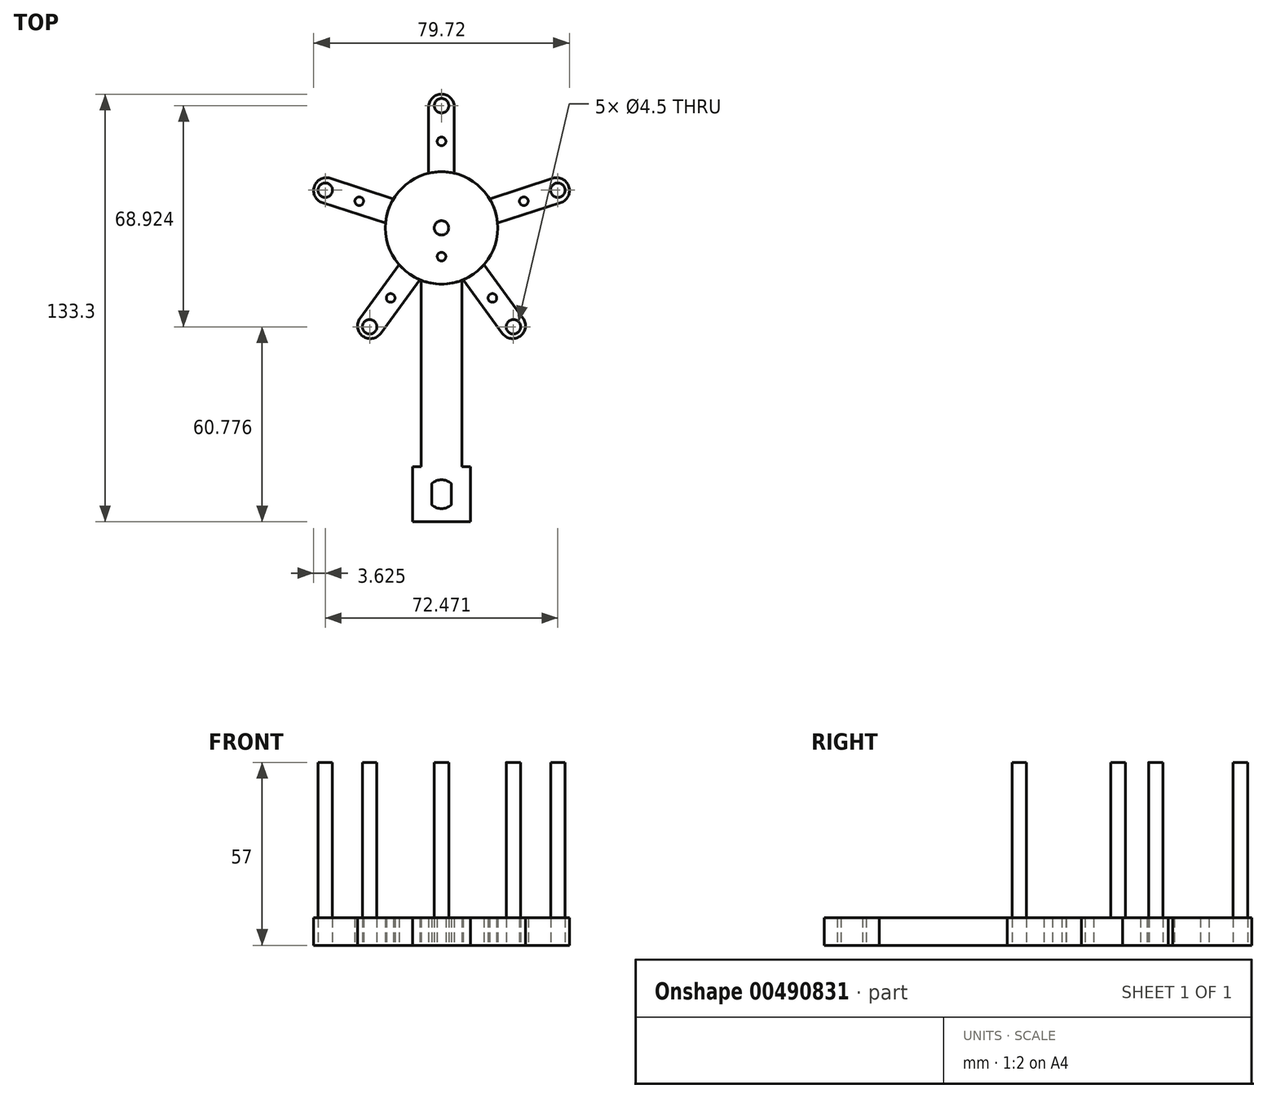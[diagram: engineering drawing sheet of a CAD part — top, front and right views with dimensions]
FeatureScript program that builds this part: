
annotation { "Feature Type Name" : "Feature", "Feature Type Description" : "" }
export const myFeature = defineFeature(function(context is Context, id is Id, definition is map)
    precondition{}
    {
        {
            var Q0;
            Q0=qCreatedBy(makeId("Top.planeOp"),FACE);
            var sketch = newSketch(context, id + "F0", { "sketchPlane" : qUnion([Q0])});
            skCircle(sketch, "E0", {"center": v(0, 0) * mm, "radius": 17.5 * mm});
            skLineSegment(sketch, "E1", {"start": v(-4, 41.7) * mm, "end": v(0, 41.7) * mm});
            skLineSegment(sketch, "E2", {"start": v(0, 41.7) * mm, "end": v(4, 41.7) * mm});
            skLineSegment(sketch, "E3", {"start": v(-6.35, -16.3) * mm, "end": v(-6.35, -74.4) * mm});
            skLineSegment(sketch, "E4", {"start": v(-6.35, -74.4) * mm, "end": v(0, -74.4) * mm});
            skLineSegment(sketch, "E5", {"start": v(0, -74.4) * mm, "end": v(6.35, -74.4) * mm});
            skLineSegment(sketch, "E6", {"start": v(6.35, -74.4) * mm, "end": v(6.35, -16.3) * mm});
            skLineSegment(sketch, "E7.bottom", {"start": v(9, -74.4) * mm, "end": v(-9, -74.4) * mm});
            skLineSegment(sketch, "E7.top", {"start": v(9, -91.6) * mm, "end": v(-9, -91.6) * mm});
            skLineSegment(sketch, "E7.left", {"start": v(9, -74.4) * mm, "end": v(9, -91.6) * mm});
            skLineSegment(sketch, "E7.right", {"start": v(-9, -74.4) * mm, "end": v(-9, -91.6) * mm});
            skPoint(sketch, "E7.middle", {"position": v(0, -83) * mm});
            skLineSegment(sketch, "E8.left", {"start": v(3, -86.35) * mm, "end": v(3, -79.65) * mm});
            skLineSegment(sketch, "E8.right", {"start": v(-3, -86.35) * mm, "end": v(-3, -79.65) * mm});
            skCircle(sketch, "E9", {"center": v(0, 38.1) * mm, "radius": 2.25 * mm});
            skLineSegment(sketch, "E10", {"start": v(4, 41.7) * mm, "end": v(4, 17.04) * mm});
            skLineSegment(sketch, "E11", {"start": v(-4, 41.7) * mm, "end": v(-4, 17.04) * mm});
            skCircle(sketch, "E12", {"center": v(-0.01, 0.01) * mm, "radius": 2.25 * mm});
            skArc(sketch, "E13", {"start": v(-3, -86.35) * mm, "mid": v(0, -87.5) * mm, "end": v(3, -86.35) * mm});
            skPoint(sketch, "E14.orphan", {"position": v(-3, -78.24) * mm});
            skPoint(sketch, "E15.orphan", {"position": v(-3, -87.33) * mm});
            skPoint(sketch, "E16.orphan", {"position": v(3, -87.76) * mm});
            skArc(sketch, "E17.trimOffspring", {"start": v(3, -79.65) * mm, "mid": v(0, -78.5) * mm, "end": v(-3, -79.65) * mm});
            skPoint(sketch, "E8.top.start.orphan", {"position": v(3, -78.67) * mm});
            skCircle(sketch, "E18", {"center": v(0, -8.94) * mm, "radius": 1.35 * mm});
            skCircle(sketch, "E19", {"center": v(0, 26.97) * mm, "radius": 1.35 * mm});
            skSolve(sketch);
        }
        {
            var Q0;
            {var subQ0=sQuery(id+"F0.wireOp",EDGE,"R38fcb1h-lACT-zBL9-eRLb-SoO7664i7xEH");Q0=makeQuery(id+"F0.imprint","IMPRINT",FACE,{"disambiguationData":[TD([[makeQuery(id+"F0.imprint","IMPRINT",EDGE,{"derivedFrom":subQ0}),-1.0]])]});}
            var Q1;
            {var subQ0=sQuery(id+"F0.wireOp",EDGE,"E0");var subQ1=makeQuery(id+"F0.imprint","INTERSECT",VERTEX,{"derivedFrom":[subQ0,sQuery(id+"F0.wireOp",EDGE,"R38fcb1h-lACT-zBL9-eRLb-SoO7664i7xEH")]});Q1=makeQuery(id+"F0.imprint","IMPRINT",FACE,{"disambiguationData":[TD([[makeQuery(id+"F0.imprint","IMPRINT",EDGE,{"disambiguationData":[TD([[subQ1,1.0]])],"derivedFrom":subQ0}),1.0]])]});}
            extrude(context, id + "F1", {"entities" : qUnion([Q0, Q1]), "depth" : 8.6 * mm});
        }
        {
            var Q0;
            {var subQ0=sQuery(id+"F0.wireOp",EDGE,"E3");Q0=makeQuery(id+"F0.imprint","IMPRINT",FACE,{"disambiguationData":[TD([[makeQuery(id+"F0.imprint","IMPRINT",EDGE,{"derivedFrom":subQ0}),1.0]])]});}
            var Q1;
            Q1=makeQuery(id+"F0.imprint","IMPRINT",FACE,{"disambiguationData":[TD([[makeQuery(id+"F0.imprint","IMPRINT",EDGE,{"derivedFrom":sQuery(id+"F0.wireOp",EDGE,"E7.top")}),-1.0]])]});
            extrude(context, id + "F2", {"entities" : qUnion([Q0, Q1]), "depth" : 8.6 * mm});
        }
        {
            var Q0;
            Q0=makeQuery(id+"F0.imprint","IMPRINT",FACE,{"disambiguationData":[TD([[makeQuery(id+"F0.imprint","IMPRINT",EDGE,{"derivedFrom":sQuery(id+"F0.wireOp",EDGE,"E9")}),1.0]])]});
            extrude(context, id + "F3", {"entities" : qUnion([Q0]), "depth" : 57 * mm, "offsetDistance" : 25 * mm});
        }
        {
            var Q0;
            Q0=makeQuery(id+"F0.imprint","IMPRINT",FACE,{"disambiguationData":[TD([[makeQuery(id+"F0.imprint","IMPRINT",EDGE,{"derivedFrom":sQuery(id+"F0.wireOp",EDGE,"E1")}),-1.0]])]});
            extrude(context, id + "F4", {"entities" : qUnion([Q0]), "depth" : 8.6 * mm, "offsetDistance" : 25 * mm});
        }
        {
            var Q0;
            Q0=makeQuery(id+"F0.imprint","IMPRINT",FACE,{"disambiguationData":[TD([[makeQuery(id+"F0.imprint","IMPRINT",EDGE,{"derivedFrom":sQuery(id+"F0.wireOp",EDGE,"E12")}),1.0]])]});
            extrude(context, id + "F5", {"entities" : qUnion([Q0]), "operationType" : NewBodyOperationType.ADD, "depth" : 57 * mm, "offsetDistance" : 25 * mm});
        }
        {
            var Q0;
            Q0=makeQuery(id+"F4.opExtrude","SWEPT_BODY",BODY,{"disambiguationData":[OSD([sQuery(id+"F0.wireOp",EDGE,"E0"),sQuery(id+"F0.wireOp",EDGE,"E1"),sQuery(id+"F0.wireOp",EDGE,"E2"),sQuery(id+"F0.wireOp",EDGE,"E9"),sQuery(id+"F0.wireOp",EDGE,"E10"),sQuery(id+"F0.wireOp",EDGE,"E11")])]});
            var Q1;
            Q1=makeQuery(id+"F3.opExtrude","SWEPT_BODY",BODY,{"disambiguationData":[OSD([sQuery(id+"F0.wireOp",EDGE,"E9")])]});
            var Q2;
            Q2=sQuery(id+"F0.wireOp",EDGE,"E0");
            circularPattern(context, id + "F6", {"entities" : qUnion([Q0, Q1]), "axis" : qUnion([Q2]), "angle" : 360 * degree, "instanceCount" : 5, "equalSpace" : true});
        }
        {
            var Q0;
            Q0=makeQuery(id+"F4.opExtrude","SWEPT_EDGE",EDGE,{"disambiguationData":[OSD([sQuery(id+"F0.wireOp",EDGE,"E1"),sQuery(id+"F0.wireOp",EDGE,"E11")])]});
            var Q1;
            Q1=makeQuery(id+"F4.opExtrude","SWEPT_EDGE",EDGE,{"disambiguationData":[OSD([sQuery(id+"F0.wireOp",EDGE,"E2"),sQuery(id+"F0.wireOp",EDGE,"E10")])]});
            var Q2;
            Q2=makeQuery(id+"F6.opPattern","COPY",EDGE,{"derivedFrom":makeQuery(id+"F4.opExtrude","SWEPT_EDGE",EDGE,{"disambiguationData":[OSD([sQuery(id+"F0.wireOp",EDGE,"E2"),sQuery(id+"F0.wireOp",EDGE,"E10")])]}),"instanceName":"1"});
            var Q3;
            Q3=makeQuery(id+"F6.opPattern","COPY",EDGE,{"derivedFrom":makeQuery(id+"F4.opExtrude","SWEPT_EDGE",EDGE,{"disambiguationData":[OSD([sQuery(id+"F0.wireOp",EDGE,"E1"),sQuery(id+"F0.wireOp",EDGE,"E11")])]}),"instanceName":"1"});
            var Q4;
            Q4=makeQuery(id+"F6.opPattern","COPY",EDGE,{"derivedFrom":makeQuery(id+"F4.opExtrude","SWEPT_EDGE",EDGE,{"disambiguationData":[OSD([sQuery(id+"F0.wireOp",EDGE,"E2"),sQuery(id+"F0.wireOp",EDGE,"E10")])]}),"instanceName":"2"});
            var Q5;
            Q5=makeQuery(id+"F6.opPattern","COPY",EDGE,{"derivedFrom":makeQuery(id+"F4.opExtrude","SWEPT_EDGE",EDGE,{"disambiguationData":[OSD([sQuery(id+"F0.wireOp",EDGE,"E1"),sQuery(id+"F0.wireOp",EDGE,"E11")])]}),"instanceName":"4"});
            var Q6;
            Q6=makeQuery(id+"F6.opPattern","COPY",EDGE,{"derivedFrom":makeQuery(id+"F4.opExtrude","SWEPT_EDGE",EDGE,{"disambiguationData":[OSD([sQuery(id+"F0.wireOp",EDGE,"E2"),sQuery(id+"F0.wireOp",EDGE,"E10")])]}),"instanceName":"4"});
            var Q7;
            Q7=makeQuery(id+"F6.opPattern","COPY",EDGE,{"derivedFrom":makeQuery(id+"F4.opExtrude","SWEPT_EDGE",EDGE,{"disambiguationData":[OSD([sQuery(id+"F0.wireOp",EDGE,"E1"),sQuery(id+"F0.wireOp",EDGE,"E11")])]}),"instanceName":"3"});
            var Q8;
            Q8=makeQuery(id+"F6.opPattern","COPY",EDGE,{"derivedFrom":makeQuery(id+"F4.opExtrude","SWEPT_EDGE",EDGE,{"disambiguationData":[OSD([sQuery(id+"F0.wireOp",EDGE,"E2"),sQuery(id+"F0.wireOp",EDGE,"E10")])]}),"instanceName":"3"});
            var Q9;
            Q9=makeQuery(id+"F6.opPattern","COPY",EDGE,{"derivedFrom":makeQuery(id+"F4.opExtrude","SWEPT_EDGE",EDGE,{"disambiguationData":[OSD([sQuery(id+"F0.wireOp",EDGE,"E1"),sQuery(id+"F0.wireOp",EDGE,"E11")])]}),"instanceName":"2"});
            fillet(context, id + "F7", {"entities" : qUnion([Q0, Q1, Q2, Q3, Q4, Q5, Q6, Q7, Q8, Q9]), "radius" : 4 * mm, "tangentPropagation" : true, "allowEdgeOverflow" : false});
        }
    });
